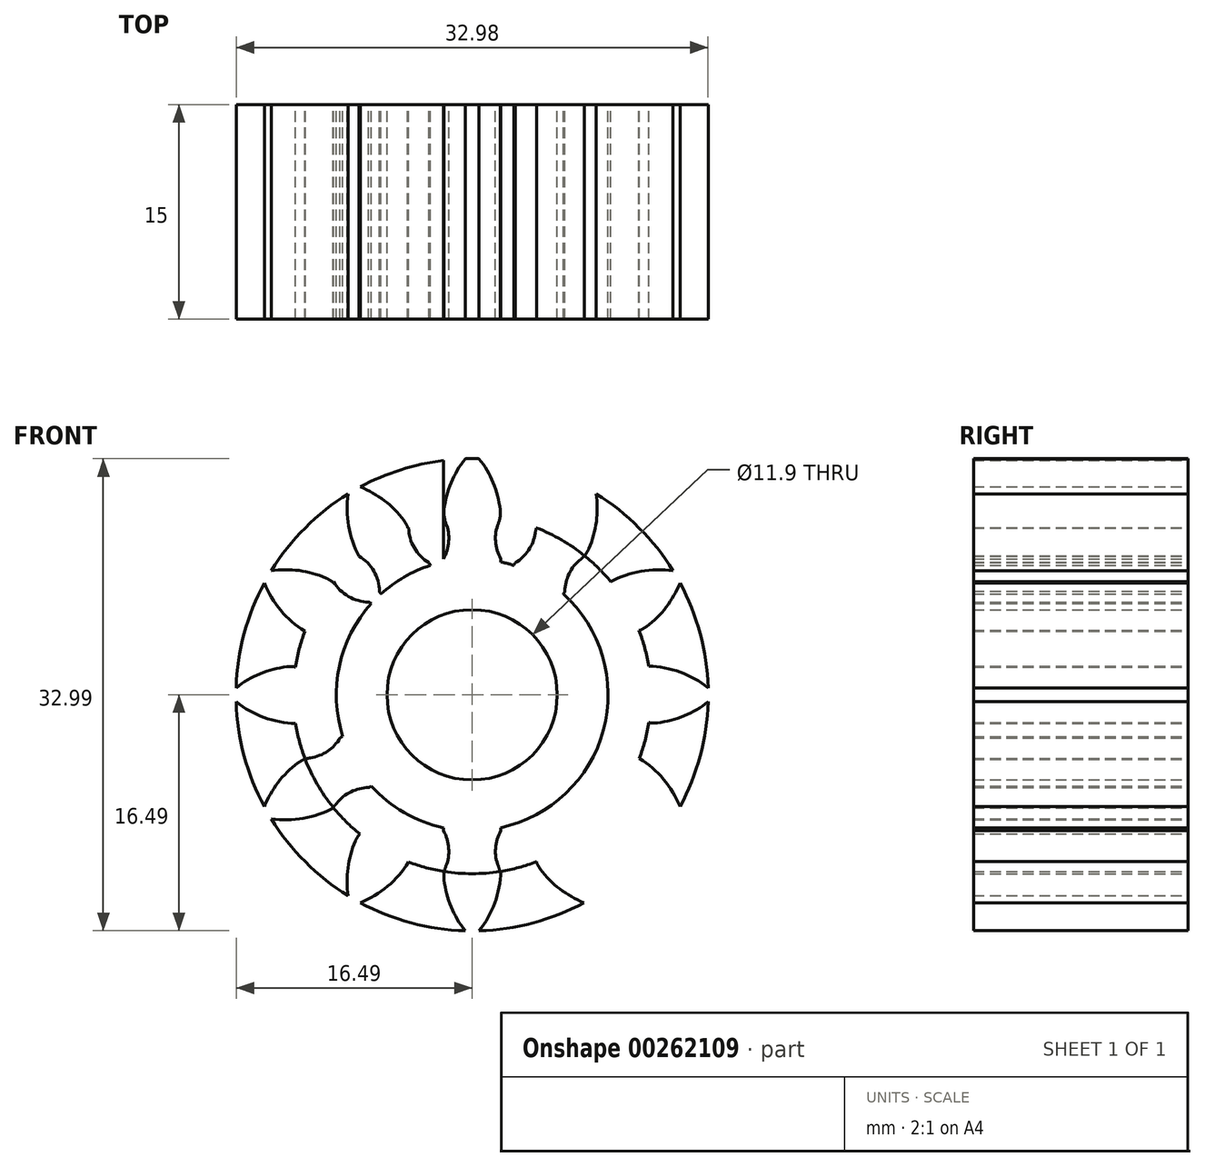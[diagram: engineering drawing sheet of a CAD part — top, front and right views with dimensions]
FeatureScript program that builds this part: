
annotation { "Feature Type Name" : "Feature", "Feature Type Description" : "" }
export const myFeature = defineFeature(function(context is Context, id is Id, definition is map)
    precondition{}
    {
        {
            var Q0;
            Q0=qCreatedBy(makeId("Front.planeOp"),FACE);
            var sketch = newSketch(context, id + "F0", { "sketchPlane" : qUnion([Q0])});
            skCircle(sketch, "E0", {"center": v(0, 0) * mm, "radius": 16.5 * mm});
            skCircle(sketch, "E1", {"center": v(0, 0) * mm, "radius": 9.5 * mm});
            skCircle(sketch, "E2", {"center": v(0, 0) * mm, "radius": 12.5 * mm});
            skLineSegment(sketch, "E3", {"start": v(0, 0) * mm, "end": v(0, 25.7) * mm, "construction": true});
            skLineSegment(sketch, "E4", {"start": v(0, 12.5) * mm, "end": v(10.82, 16.44) * mm});
            skLineSegment(sketch, "E5", {"start": v(0, 12.5) * mm, "end": v(18.32, 12.5) * mm, "construction": true});
            skLineSegment(sketch, "E6", {"start": v(0, 9.5) * mm, "end": v(-2, 9.5) * mm, "construction": true});
            skLineSegment(sketch, "E7", {"start": v(-2, 9.5) * mm, "end": v(-2, 16.38) * mm});
            skLineSegment(sketch, "E8.MirrorCS", {"start": v(2, 9.5) * mm, "end": v(2, 16.38) * mm});
            skLineSegment(sketch, "E9", {"start": v(-2, 12.34) * mm, "end": v(-5.78, 12.34) * mm, "construction": true});
            skArc(sketch, "E10.MirrorCS", {"start": v(0.49, 16.5) * mm, "mid": v(1.47, 14.82) * mm, "end": v(1.96, 12.94) * mm});
            skArc(sketch, "E11.MirrorCS", {"start": v(0.49, 16.5) * mm, "mid": v(1.42, 14.94) * mm, "end": v(1.92, 13.2) * mm});
            skArc(sketch, "E12", {"start": v(-2, 9.5) * mm, "mid": v(-1.64, 10.72) * mm, "end": v(-1.83, 11.98) * mm});
            skArc(sketch, "E13.MirrorCS", {"start": v(2, 9.5) * mm, "mid": v(1.64, 10.72) * mm, "end": v(1.83, 11.98) * mm});
            skArc(sketch, "E14.1.0", {"start": v(-6.48, 7.23) * mm, "mid": v(-6.87, 8.64) * mm, "end": v(-7.9, 9.69) * mm});
            skArc(sketch, "E14.1.1", {"start": v(-3.02, 9.23) * mm, "mid": v(-4.05, 10.27) * mm, "end": v(-4.44, 11.69) * mm});
            skArc(sketch, "E14.2.0", {"start": v(-9.23, 3.02) * mm, "mid": v(-10.27, 4.05) * mm, "end": v(-11.69, 4.44) * mm});
            skArc(sketch, "E14.2.1", {"start": v(-7.23, 6.48) * mm, "mid": v(-8.64, 6.87) * mm, "end": v(-9.69, 7.9) * mm});
            skArc(sketch, "E15.1.0", {"start": v(-6.48, -7.23) * mm, "mid": v(-6.87, -8.64) * mm, "end": v(-7.9, -9.69) * mm});
            skArc(sketch, "E15.1.2", {"start": v(-3.02, -9.23) * mm, "mid": v(-4.05, -10.27) * mm, "end": v(-4.44, -11.69) * mm});
            skArc(sketch, "E15.2.0", {"start": v(-2, -9.5) * mm, "mid": v(-1.63, -10.92) * mm, "end": v(-2, -12.34) * mm});
            skArc(sketch, "E16.8.3.0", {"start": v(6.48, -7.23) * mm, "mid": v(6.87, -8.64) * mm, "end": v(7.9, -9.69) * mm});
            skArc(sketch, "E16.14.3.0", {"start": v(3.02, -9.23) * mm, "mid": v(4.05, -10.27) * mm, "end": v(4.44, -11.69) * mm});
            skArc(sketch, "E16.4.4.0", {"start": v(14.04, -8.67) * mm, "mid": v(11.8, -8.64) * mm, "end": v(9.69, -7.9) * mm});
            skArc(sketch, "E16.8.4.0", {"start": v(9.23, -3.02) * mm, "mid": v(10.27, -4.05) * mm, "end": v(11.69, -4.44) * mm});
            skArc(sketch, "E16.14.4.0", {"start": v(7.23, -6.48) * mm, "mid": v(8.64, -6.87) * mm, "end": v(9.69, -7.9) * mm});
            skArc(sketch, "E16.8.5.0", {"start": v(9.5, 2) * mm, "mid": v(10.92, 1.63) * mm, "end": v(12.34, 2) * mm});
            skArc(sketch, "E16.14.5.0", {"start": v(9.5, -2) * mm, "mid": v(10.92, -1.63) * mm, "end": v(12.34, -2) * mm});
            skArc(sketch, "E16.8.6.0", {"start": v(7.23, 6.48) * mm, "mid": v(8.64, 6.87) * mm, "end": v(9.69, 7.9) * mm});
            skArc(sketch, "E16.14.6.0", {"start": v(9.23, 3.02) * mm, "mid": v(10.27, 4.05) * mm, "end": v(11.69, 4.44) * mm});
            skArc(sketch, "E16.14.7.0", {"start": v(6.48, 7.23) * mm, "mid": v(6.87, 8.64) * mm, "end": v(7.9, 9.69) * mm});
            skArc(sketch, "E16.8.11.0", {"start": v(-9.5, -2) * mm, "mid": v(-10.92, -1.63) * mm, "end": v(-12.34, -2) * mm});
            skArc(sketch, "E16.14.11.0", {"start": v(-9.5, 2) * mm, "mid": v(-10.92, 1.63) * mm, "end": v(-12.34, 2) * mm});
            skArc(sketch, "E17.1.2", {"start": v(-7.82, -14.53) * mm, "mid": v(-5.9, -13.38) * mm, "end": v(-4.44, -11.69) * mm});
            skArc(sketch, "E17.2.0", {"start": v(1.66, 14.47) * mm, "mid": v(2.03, 13.24) * mm, "end": v(1.83, 11.98) * mm});
            skPoint(sketch, "E18.visualSharp", {"position": v(-8.06, 20.68) * mm});
            skArc(sketch, "E18.filletArc", {"start": v(-1.96, 12.94) * mm, "mid": v(-1.95, 12.45) * mm, "end": v(-1.83, 11.98) * mm});
            skPoint(sketch, "E19.orphan", {"position": v(-2, 12.34) * mm});
            skPoint(sketch, "E20.visualSharp", {"position": v(2, 12.34) * mm});
            skArc(sketch, "E20.filletArc", {"start": v(1.83, 11.98) * mm, "mid": v(1.95, 12.45) * mm, "end": v(1.96, 12.94) * mm});
            skPoint(sketch, "E21.orphan", {"position": v(1.66, 11.63) * mm});
            skPoint(sketch, "E22.start.orphan", {"position": v(-0.49, 16.5) * mm});
            skArc(sketch, "E23.4.3.0", {"start": v(-16.5, 0.49) * mm, "mid": v(-14.94, 1.42) * mm, "end": v(-13.2, 1.92) * mm});
            skArc(sketch, "E23.8.3.0", {"start": v(-9.5, 2) * mm, "mid": v(-10.72, 1.64) * mm, "end": v(-11.98, 1.83) * mm});
            skPoint(sketch, "E23.11.3.0", {"position": v(-12.34, 2) * mm});
            skArc(sketch, "E23.12.3.0", {"start": v(-9.5, -2) * mm, "mid": v(-10.72, -1.64) * mm, "end": v(-11.98, -1.83) * mm});
            skArc(sketch, "E23.4.4.0", {"start": v(-14.53, -7.82) * mm, "mid": v(-13.65, -6.24) * mm, "end": v(-12.4, -4.93) * mm});
            skArc(sketch, "E23.8.4.0", {"start": v(-9.23, -3.02) * mm, "mid": v(-10.1, -3.94) * mm, "end": v(-11.3, -4.4) * mm});
            skPoint(sketch, "E23.11.4.0", {"position": v(-11.69, -4.44) * mm});
            skArc(sketch, "E23.12.4.0", {"start": v(-7.23, -6.48) * mm, "mid": v(-8.47, -6.78) * mm, "end": v(-9.46, -7.58) * mm});
            skArc(sketch, "E23.4.5.0", {"start": v(-8.67, -14.04) * mm, "mid": v(-8.7, -12.23) * mm, "end": v(-8.27, -10.47) * mm});
            skArc(sketch, "E23.8.5.0", {"start": v(-6.48, -7.23) * mm, "mid": v(-6.78, -8.47) * mm, "end": v(-7.58, -9.46) * mm});
            skPoint(sketch, "E23.11.5.0", {"position": v(-7.9, -9.69) * mm});
            skArc(sketch, "E23.12.5.0", {"start": v(-3.02, -9.23) * mm, "mid": v(-3.94, -10.1) * mm, "end": v(-4.4, -11.3) * mm});
            skArc(sketch, "E23.4.6.0", {"start": v(-0.49, -16.5) * mm, "mid": v(-1.42, -14.94) * mm, "end": v(-1.92, -13.2) * mm});
            skArc(sketch, "E23.8.6.0", {"start": v(-2, -9.5) * mm, "mid": v(-1.64, -10.72) * mm, "end": v(-1.83, -11.98) * mm});
            skPoint(sketch, "E23.11.6.0", {"position": v(-2, -12.34) * mm});
            skArc(sketch, "E23.12.6.0", {"start": v(2, -9.5) * mm, "mid": v(1.64, -10.72) * mm, "end": v(1.83, -11.98) * mm});
            skArc(sketch, "E23.4.7.0", {"start": v(7.82, -14.53) * mm, "mid": v(6.24, -13.65) * mm, "end": v(4.93, -12.4) * mm});
            skArc(sketch, "E23.8.7.0", {"start": v(3.02, -9.23) * mm, "mid": v(3.94, -10.1) * mm, "end": v(4.4, -11.3) * mm});
            skPoint(sketch, "E23.11.7.0", {"position": v(4.44, -11.69) * mm});
            skArc(sketch, "E23.12.7.0", {"start": v(6.48, -7.23) * mm, "mid": v(6.78, -8.47) * mm, "end": v(7.58, -9.46) * mm});
            skArc(sketch, "E23.4.8.0", {"start": v(14.04, -8.67) * mm, "mid": v(12.23, -8.7) * mm, "end": v(10.47, -8.27) * mm});
            skArc(sketch, "E23.8.8.0", {"start": v(7.23, -6.48) * mm, "mid": v(8.47, -6.78) * mm, "end": v(9.46, -7.58) * mm});
            skPoint(sketch, "E23.11.8.0", {"position": v(9.69, -7.9) * mm});
            skArc(sketch, "E23.12.8.0", {"start": v(9.23, -3.02) * mm, "mid": v(10.1, -3.94) * mm, "end": v(11.3, -4.4) * mm});
            skArc(sketch, "E23.4.9.0", {"start": v(16.5, -0.49) * mm, "mid": v(14.94, -1.42) * mm, "end": v(13.2, -1.92) * mm});
            skArc(sketch, "E23.8.9.0", {"start": v(9.5, -2) * mm, "mid": v(10.72, -1.64) * mm, "end": v(11.98, -1.83) * mm});
            skPoint(sketch, "E23.11.9.0", {"position": v(12.34, -2) * mm});
            skArc(sketch, "E23.12.9.0", {"start": v(9.5, 2) * mm, "mid": v(10.72, 1.64) * mm, "end": v(11.98, 1.83) * mm});
            skArc(sketch, "E23.4.10.0", {"start": v(14.53, 7.82) * mm, "mid": v(13.65, 6.24) * mm, "end": v(12.4, 4.93) * mm});
            skArc(sketch, "E23.8.10.0", {"start": v(9.23, 3.02) * mm, "mid": v(10.1, 3.94) * mm, "end": v(11.3, 4.4) * mm});
            skPoint(sketch, "E23.11.10.0", {"position": v(11.69, 4.44) * mm});
            skArc(sketch, "E23.12.10.0", {"start": v(7.23, 6.48) * mm, "mid": v(8.47, 6.78) * mm, "end": v(9.46, 7.58) * mm});
            skArc(sketch, "E23.4.11.0", {"start": v(8.67, 14.04) * mm, "mid": v(8.7, 12.23) * mm, "end": v(8.27, 10.47) * mm});
            skArc(sketch, "E23.8.11.0", {"start": v(6.48, 7.23) * mm, "mid": v(6.78, 8.47) * mm, "end": v(7.58, 9.46) * mm});
            skPoint(sketch, "E23.11.11.0", {"position": v(7.9, 9.69) * mm});
            skArc(sketch, "E23.12.11.0", {"start": v(3.02, 9.23) * mm, "mid": v(3.94, 10.1) * mm, "end": v(4.4, 11.3) * mm});
            skArc(sketch, "E24.4.3.0", {"start": v(-7.82, 14.53) * mm, "mid": v(-6.24, 13.65) * mm, "end": v(-4.93, 12.4) * mm});
            skArc(sketch, "E24.8.3.0", {"start": v(-14.04, -8.67) * mm, "mid": v(-11.8, -8.64) * mm, "end": v(-9.69, -7.9) * mm});
            skArc(sketch, "E24.4.4.0", {"start": v(-14.04, 8.67) * mm, "mid": v(-12.23, 8.7) * mm, "end": v(-10.47, 8.27) * mm});
            skArc(sketch, "E24.8.5.0", {"start": v(0.49, -16.5) * mm, "mid": v(1.58, -14.54) * mm, "end": v(2, -12.34) * mm});
            skArc(sketch, "E24.8.6.0", {"start": v(8.67, -14.04) * mm, "mid": v(8.64, -11.8) * mm, "end": v(7.9, -9.69) * mm});
            skArc(sketch, "E24.8.7.0", {"start": v(14.53, -7.82) * mm, "mid": v(13.38, -5.9) * mm, "end": v(11.69, -4.44) * mm});
            skArc(sketch, "E24.12.7.0", {"start": v(3.02, 9.23) * mm, "mid": v(4.05, 10.27) * mm, "end": v(4.44, 11.69) * mm});
            skArc(sketch, "E24.8.8.0", {"start": v(16.5, 0.49) * mm, "mid": v(14.54, 1.58) * mm, "end": v(12.34, 2) * mm});
            skArc(sketch, "E24.10.8.0", {"start": v(2, 9.5) * mm, "mid": v(1.63, 10.92) * mm, "end": v(2, 12.34) * mm});
            skArc(sketch, "E24.12.8.0", {"start": v(-2, 9.5) * mm, "mid": v(-1.63, 10.92) * mm, "end": v(-2, 12.34) * mm});
            skArc(sketch, "E24.8.9.0", {"start": v(14.04, 8.67) * mm, "mid": v(11.8, 8.64) * mm, "end": v(9.69, 7.9) * mm});
            skArc(sketch, "E24.8.10.0", {"start": v(7.82, 14.53) * mm, "mid": v(5.9, 13.38) * mm, "end": v(4.44, 11.69) * mm});
            skArc(sketch, "E24.8.11.0", {"start": v(-0.49, 16.5) * mm, "mid": v(-1.58, 14.54) * mm, "end": v(-2, 12.34) * mm});
            skArc(sketch, "E25.1.2", {"start": v(-8.17, 10.23) * mm, "mid": v(-7.92, 9.8) * mm, "end": v(-7.58, 9.46) * mm});
            skArc(sketch, "E25.1.3", {"start": v(-4.4, 11.3) * mm, "mid": v(-4.54, 11.76) * mm, "end": v(-4.78, 12.19) * mm});
            skArc(sketch, "E25.1.4", {"start": v(-7.82, 14.53) * mm, "mid": v(-6.14, 13.57) * mm, "end": v(-4.78, 12.19) * mm});
            skArc(sketch, "E25.1.5", {"start": v(-8.67, 14.04) * mm, "mid": v(-8.64, 11.8) * mm, "end": v(-7.9, 9.69) * mm});
            skArc(sketch, "E25.2.2", {"start": v(-12.19, 4.78) * mm, "mid": v(-11.76, 4.54) * mm, "end": v(-11.3, 4.4) * mm});
            skArc(sketch, "E25.2.3", {"start": v(-9.46, 7.58) * mm, "mid": v(-9.8, 7.92) * mm, "end": v(-10.23, 8.17) * mm});
            skArc(sketch, "E25.2.4", {"start": v(-14.04, 8.67) * mm, "mid": v(-12.1, 8.68) * mm, "end": v(-10.23, 8.17) * mm});
            skArc(sketch, "E25.2.5", {"start": v(-14.53, 7.82) * mm, "mid": v(-13.38, 5.9) * mm, "end": v(-11.69, 4.44) * mm});
            skArc(sketch, "E25.3.2", {"start": v(-12.94, -1.96) * mm, "mid": v(-12.45, -1.95) * mm, "end": v(-11.98, -1.83) * mm});
            skArc(sketch, "E25.3.3", {"start": v(-11.98, 1.83) * mm, "mid": v(-12.45, 1.95) * mm, "end": v(-12.94, 1.96) * mm});
            skArc(sketch, "E25.3.4", {"start": v(-16.5, 0.49) * mm, "mid": v(-14.82, 1.47) * mm, "end": v(-12.94, 1.96) * mm});
            skArc(sketch, "E25.3.5", {"start": v(-16.5, -0.49) * mm, "mid": v(-14.54, -1.58) * mm, "end": v(-12.34, -2) * mm});
            skArc(sketch, "E25.4.2", {"start": v(-10.23, -8.17) * mm, "mid": v(-9.8, -7.92) * mm, "end": v(-9.46, -7.58) * mm});
            skArc(sketch, "E25.4.3", {"start": v(-11.3, -4.4) * mm, "mid": v(-11.76, -4.54) * mm, "end": v(-12.19, -4.78) * mm});
            skArc(sketch, "E25.4.4", {"start": v(-14.53, -7.82) * mm, "mid": v(-13.57, -6.14) * mm, "end": v(-12.19, -4.78) * mm});
            skArc(sketch, "E25.5.2", {"start": v(-4.78, -12.19) * mm, "mid": v(-4.54, -11.76) * mm, "end": v(-4.4, -11.3) * mm});
            skArc(sketch, "E25.5.3", {"start": v(-7.58, -9.46) * mm, "mid": v(-7.92, -9.8) * mm, "end": v(-8.17, -10.23) * mm});
            skArc(sketch, "E25.5.4", {"start": v(-8.67, -14.04) * mm, "mid": v(-8.68, -12.1) * mm, "end": v(-8.17, -10.23) * mm});
            skArc(sketch, "E25.6.2", {"start": v(1.96, -12.94) * mm, "mid": v(1.95, -12.45) * mm, "end": v(1.83, -11.98) * mm});
            skArc(sketch, "E25.6.3", {"start": v(-1.83, -11.98) * mm, "mid": v(-1.95, -12.45) * mm, "end": v(-1.96, -12.94) * mm});
            skArc(sketch, "E25.6.4", {"start": v(-0.49, -16.5) * mm, "mid": v(-1.47, -14.82) * mm, "end": v(-1.96, -12.94) * mm});
            skArc(sketch, "E25.7.2", {"start": v(8.17, -10.23) * mm, "mid": v(7.92, -9.8) * mm, "end": v(7.58, -9.46) * mm});
            skArc(sketch, "E25.7.3", {"start": v(4.4, -11.3) * mm, "mid": v(4.54, -11.76) * mm, "end": v(4.78, -12.19) * mm});
            skArc(sketch, "E25.7.4", {"start": v(7.82, -14.53) * mm, "mid": v(6.14, -13.57) * mm, "end": v(4.78, -12.19) * mm});
            skArc(sketch, "E25.8.2", {"start": v(12.19, -4.78) * mm, "mid": v(11.76, -4.54) * mm, "end": v(11.3, -4.4) * mm});
            skArc(sketch, "E25.8.3", {"start": v(9.46, -7.58) * mm, "mid": v(9.8, -7.92) * mm, "end": v(10.23, -8.17) * mm});
            skArc(sketch, "E25.8.4", {"start": v(14.04, -8.67) * mm, "mid": v(12.1, -8.68) * mm, "end": v(10.23, -8.17) * mm});
            skArc(sketch, "E25.9.2", {"start": v(12.94, 1.96) * mm, "mid": v(12.45, 1.95) * mm, "end": v(11.98, 1.83) * mm});
            skArc(sketch, "E25.9.3", {"start": v(11.98, -1.83) * mm, "mid": v(12.45, -1.95) * mm, "end": v(12.94, -1.96) * mm});
            skArc(sketch, "E25.9.4", {"start": v(16.5, -0.49) * mm, "mid": v(14.82, -1.47) * mm, "end": v(12.94, -1.96) * mm});
            skArc(sketch, "E25.10.2", {"start": v(10.23, 8.17) * mm, "mid": v(9.8, 7.92) * mm, "end": v(9.46, 7.58) * mm});
            skArc(sketch, "E25.10.3", {"start": v(11.3, 4.4) * mm, "mid": v(11.76, 4.54) * mm, "end": v(12.19, 4.78) * mm});
            skArc(sketch, "E25.10.4", {"start": v(14.53, 7.82) * mm, "mid": v(13.57, 6.14) * mm, "end": v(12.19, 4.78) * mm});
            skArc(sketch, "E25.11.2", {"start": v(4.78, 12.19) * mm, "mid": v(4.54, 11.76) * mm, "end": v(4.4, 11.3) * mm});
            skArc(sketch, "E25.11.3", {"start": v(7.58, 9.46) * mm, "mid": v(7.92, 9.8) * mm, "end": v(8.17, 10.23) * mm});
            skArc(sketch, "E25.11.4", {"start": v(8.67, 14.04) * mm, "mid": v(8.68, 12.1) * mm, "end": v(8.17, 10.23) * mm});
            skArc(sketch, "E26", {"start": v(-2, 9.5) * mm, "mid": v(-2, 9.4) * mm, "end": v(-2, 9.29) * mm});
            skArc(sketch, "E27.MirrorCS", {"start": v(2, 9.5) * mm, "mid": v(2, 9.4) * mm, "end": v(2, 9.29) * mm});
            skArc(sketch, "E28.1.0", {"start": v(-3.02, 9.23) * mm, "mid": v(-2.96, 9.14) * mm, "end": v(-2.91, 9.04) * mm});
            skArc(sketch, "E28.1.1", {"start": v(-6.48, 7.23) * mm, "mid": v(-6.44, 7.13) * mm, "end": v(-6.38, 7.04) * mm});
            skArc(sketch, "E28.2.0", {"start": v(-7.23, 6.48) * mm, "mid": v(-7.13, 6.44) * mm, "end": v(-7.04, 6.38) * mm});
            skArc(sketch, "E28.2.1", {"start": v(-9.23, 3.02) * mm, "mid": v(-9.14, 2.96) * mm, "end": v(-9.04, 2.91) * mm});
            skArc(sketch, "E28.3.0", {"start": v(-9.5, 2) * mm, "mid": v(-9.4, 2) * mm, "end": v(-9.29, 2) * mm});
            skArc(sketch, "E28.3.1", {"start": v(-9.5, -2) * mm, "mid": v(-9.4, -2) * mm, "end": v(-9.29, -2) * mm});
            skArc(sketch, "E28.4.0", {"start": v(-9.23, -3.02) * mm, "mid": v(-9.14, -2.96) * mm, "end": v(-9.04, -2.91) * mm});
            skArc(sketch, "E28.4.1", {"start": v(-7.23, -6.48) * mm, "mid": v(-7.13, -6.44) * mm, "end": v(-7.04, -6.38) * mm});
            skArc(sketch, "E28.5.0", {"start": v(-6.48, -7.23) * mm, "mid": v(-6.44, -7.13) * mm, "end": v(-6.38, -7.04) * mm});
            skArc(sketch, "E28.5.1", {"start": v(-3.02, -9.23) * mm, "mid": v(-2.96, -9.14) * mm, "end": v(-2.91, -9.04) * mm});
            skArc(sketch, "E28.6.0", {"start": v(-2, -9.5) * mm, "mid": v(-2, -9.4) * mm, "end": v(-2, -9.29) * mm});
            skArc(sketch, "E28.6.1", {"start": v(2, -9.5) * mm, "mid": v(2, -9.4) * mm, "end": v(2, -9.29) * mm});
            skArc(sketch, "E28.7.0", {"start": v(3.02, -9.23) * mm, "mid": v(2.96, -9.14) * mm, "end": v(2.91, -9.04) * mm});
            skArc(sketch, "E28.7.1", {"start": v(6.48, -7.23) * mm, "mid": v(6.44, -7.13) * mm, "end": v(6.38, -7.04) * mm});
            skArc(sketch, "E28.8.0", {"start": v(7.23, -6.48) * mm, "mid": v(7.13, -6.44) * mm, "end": v(7.04, -6.38) * mm});
            skArc(sketch, "E28.8.1", {"start": v(9.23, -3.02) * mm, "mid": v(9.14, -2.96) * mm, "end": v(9.04, -2.91) * mm});
            skArc(sketch, "E28.9.0", {"start": v(9.5, -2) * mm, "mid": v(9.4, -2) * mm, "end": v(9.29, -2) * mm});
            skArc(sketch, "E28.9.1", {"start": v(9.5, 2) * mm, "mid": v(9.4, 2) * mm, "end": v(9.29, 2) * mm});
            skArc(sketch, "E28.10.0", {"start": v(9.23, 3.02) * mm, "mid": v(9.14, 2.96) * mm, "end": v(9.04, 2.91) * mm});
            skArc(sketch, "E28.10.1", {"start": v(7.23, 6.48) * mm, "mid": v(7.13, 6.44) * mm, "end": v(7.04, 6.38) * mm});
            skArc(sketch, "E28.11.0", {"start": v(6.48, 7.23) * mm, "mid": v(6.44, 7.13) * mm, "end": v(6.38, 7.04) * mm});
            skArc(sketch, "E28.11.1", {"start": v(3.02, 9.23) * mm, "mid": v(2.96, 9.14) * mm, "end": v(2.91, 9.04) * mm});
            skCircle(sketch, "E29", {"center": v(0, 0) * mm, "radius": 5.95 * mm});
            skSolve(sketch);
        }
        {
            var Q0;
            Q0=makeQuery(id+"F0.imprint","IMPRINT",FACE,{"disambiguationData":[TD([[makeQuery(id+"F0.imprint","IMPRINT",EDGE,{"derivedFrom":sQuery(id+"F0.wireOp",EDGE,"E29")}),-1.0]])]});
            var Q1;
            {var subQ5=sQuery(id+"F0.wireOp",EDGE,"E28.2.0");Q1=makeQuery(id+"F0.imprint","IMPRINT",FACE,{"disambiguationData":[TD([[makeQuery(id+"F0.imprint","IMPRINT",EDGE,{"derivedFrom":subQ5}),-1.0]])]});}
            var Q2;
            {var subQ6=sQuery(id+"F0.wireOp",EDGE,"E28.1.0");Q2=makeQuery(id+"F0.imprint","IMPRINT",FACE,{"disambiguationData":[TD([[makeQuery(id+"F0.imprint","IMPRINT",EDGE,{"derivedFrom":subQ6}),-1.0]])]});}
            var Q3;
            {var subQ11=sQuery(id+"F0.wireOp",EDGE,"E26");Q3=makeQuery(id+"F0.imprint","IMPRINT",FACE,{"disambiguationData":[TD([[makeQuery(id+"F0.imprint","IMPRINT",EDGE,{"derivedFrom":subQ11}),1.0]])]});}
            var Q4;
            {var subQ1=sQuery(id+"F0.wireOp",EDGE,"E23.12.11.0");Q4=makeQuery(id+"F0.imprint","IMPRINT",FACE,{"disambiguationData":[TD([[makeQuery(id+"F0.imprint","IMPRINT",EDGE,{"derivedFrom":subQ1}),-1.0]])]});}
            var Q5;
            {var subQ1=sQuery(id+"F0.wireOp",EDGE,"E23.12.10.0");Q5=makeQuery(id+"F0.imprint","IMPRINT",FACE,{"disambiguationData":[TD([[makeQuery(id+"F0.imprint","IMPRINT",EDGE,{"derivedFrom":subQ1}),-1.0]])]});}
            var Q6;
            {var subQ1=sQuery(id+"F0.wireOp",EDGE,"E23.12.9.0");Q6=makeQuery(id+"F0.imprint","IMPRINT",FACE,{"disambiguationData":[TD([[makeQuery(id+"F0.imprint","IMPRINT",EDGE,{"derivedFrom":subQ1}),-1.0]])]});}
            var Q7;
            {var subQ1=sQuery(id+"F0.wireOp",EDGE,"E23.12.8.0");Q7=makeQuery(id+"F0.imprint","IMPRINT",FACE,{"disambiguationData":[TD([[makeQuery(id+"F0.imprint","IMPRINT",EDGE,{"derivedFrom":subQ1}),-1.0]])]});}
            var Q8;
            {var subQ2=sQuery(id+"F0.wireOp",EDGE,"E23.12.7.0");Q8=makeQuery(id+"F0.imprint","IMPRINT",FACE,{"disambiguationData":[TD([[makeQuery(id+"F0.imprint","IMPRINT",EDGE,{"derivedFrom":subQ2}),-1.0]])]});}
            var Q9;
            {var subQ1=sQuery(id+"F0.wireOp",EDGE,"E23.12.6.0");Q9=makeQuery(id+"F0.imprint","IMPRINT",FACE,{"disambiguationData":[TD([[makeQuery(id+"F0.imprint","IMPRINT",EDGE,{"derivedFrom":subQ1}),-1.0]])]});}
            var Q10;
            {var subQ1=sQuery(id+"F0.wireOp",EDGE,"E23.12.5.0");Q10=makeQuery(id+"F0.imprint","IMPRINT",FACE,{"disambiguationData":[TD([[makeQuery(id+"F0.imprint","IMPRINT",EDGE,{"derivedFrom":subQ1}),-1.0]])]});}
            var Q11;
            {var subQ1=sQuery(id+"F0.wireOp",EDGE,"E23.12.4.0");Q11=makeQuery(id+"F0.imprint","IMPRINT",FACE,{"disambiguationData":[TD([[makeQuery(id+"F0.imprint","IMPRINT",EDGE,{"derivedFrom":subQ1}),-1.0]])]});}
            var Q12;
            {var subQ1=sQuery(id+"F0.wireOp",EDGE,"E23.12.3.0");Q12=makeQuery(id+"F0.imprint","IMPRINT",FACE,{"disambiguationData":[TD([[makeQuery(id+"F0.imprint","IMPRINT",EDGE,{"derivedFrom":subQ1}),-1.0]])]});}
            var Q13;
            {var subQ0=sQuery(id+"F0.wireOp",EDGE,"E25.3.4");var subQ12=makeQuery(id+"F0.imprint","IMPRINT",VERTEX,{"derivedFrom":subQ0});Q13=makeQuery(id+"F0.imprint","IMPRINT",FACE,{"disambiguationData":[TD([[makeQuery(id+"F0.imprint","IMPRINT",EDGE,{"disambiguationData":[TD([[subQ12,1.0]])],"derivedFrom":subQ0}),-1.0]])]});}
            var Q14;
            {var subQ0=sQuery(id+"F0.wireOp",EDGE,"E25.2.4");var subQ12=makeQuery(id+"F0.imprint","IMPRINT",VERTEX,{"derivedFrom":subQ0});Q14=makeQuery(id+"F0.imprint","IMPRINT",FACE,{"disambiguationData":[TD([[makeQuery(id+"F0.imprint","IMPRINT",EDGE,{"disambiguationData":[TD([[subQ12,1.0]])],"derivedFrom":subQ0}),-1.0]])]});}
            var Q15;
            {var subQ0=sQuery(id+"F0.wireOp",EDGE,"E25.1.4");var subQ12=makeQuery(id+"F0.imprint","IMPRINT",VERTEX,{"derivedFrom":subQ0});Q15=makeQuery(id+"F0.imprint","IMPRINT",FACE,{"disambiguationData":[TD([[makeQuery(id+"F0.imprint","IMPRINT",EDGE,{"disambiguationData":[TD([[subQ12,1.0]])],"derivedFrom":subQ0}),-1.0]])]});}
            var Q16;
            {var subQ3=sQuery(id+"F0.wireOp",EDGE,"E2");var subQ5=sQuery(id+"F0.wireOp",EDGE,"E4");var subQ6=makeQuery(id+"F0.imprint","INTERSECT",VERTEX,{"derivedFrom":[subQ3,subQ5]});Q16=makeQuery(id+"F0.imprint","IMPRINT",FACE,{"disambiguationData":[TD([[makeQuery(id+"F0.imprint","IMPRINT",EDGE,{"disambiguationData":[TD([[subQ6,-1.0]])],"derivedFrom":subQ3}),-1.0]])]});}
            var Q17;
            {var subQ0=sQuery(id+"F0.wireOp",EDGE,"E25.11.4");var subQ12=makeQuery(id+"F0.imprint","IMPRINT",VERTEX,{"derivedFrom":subQ0});Q17=makeQuery(id+"F0.imprint","IMPRINT",FACE,{"disambiguationData":[TD([[makeQuery(id+"F0.imprint","IMPRINT",EDGE,{"disambiguationData":[TD([[subQ12,1.0]])],"derivedFrom":subQ0}),-1.0]])]});}
            var Q18;
            {var subQ5=sQuery(id+"F0.wireOp",EDGE,"E25.10.4");var subQ12=makeQuery(id+"F0.imprint","IMPRINT",VERTEX,{"derivedFrom":subQ5});Q18=makeQuery(id+"F0.imprint","IMPRINT",FACE,{"disambiguationData":[TD([[makeQuery(id+"F0.imprint","IMPRINT",EDGE,{"disambiguationData":[TD([[subQ12,1.0]])],"derivedFrom":subQ5}),-1.0]])]});}
            var Q19;
            {var subQ0=sQuery(id+"F0.wireOp",EDGE,"E25.9.4");var subQ12=makeQuery(id+"F0.imprint","IMPRINT",VERTEX,{"derivedFrom":subQ0});Q19=makeQuery(id+"F0.imprint","IMPRINT",FACE,{"disambiguationData":[TD([[makeQuery(id+"F0.imprint","IMPRINT",EDGE,{"disambiguationData":[TD([[subQ12,1.0]])],"derivedFrom":subQ0}),-1.0]])]});}
            var Q20;
            {var subQ0=sQuery(id+"F0.wireOp",EDGE,"E25.8.4");var subQ12=makeQuery(id+"F0.imprint","IMPRINT",VERTEX,{"derivedFrom":subQ0});Q20=makeQuery(id+"F0.imprint","IMPRINT",FACE,{"disambiguationData":[TD([[makeQuery(id+"F0.imprint","IMPRINT",EDGE,{"disambiguationData":[TD([[subQ12,1.0]])],"derivedFrom":subQ0}),-1.0]])]});}
            var Q21;
            {var subQ0=sQuery(id+"F0.wireOp",EDGE,"E25.7.4");var subQ12=makeQuery(id+"F0.imprint","IMPRINT",VERTEX,{"derivedFrom":subQ0});Q21=makeQuery(id+"F0.imprint","IMPRINT",FACE,{"disambiguationData":[TD([[makeQuery(id+"F0.imprint","IMPRINT",EDGE,{"disambiguationData":[TD([[subQ12,1.0]])],"derivedFrom":subQ0}),-1.0]])]});}
            var Q22;
            {var subQ0=sQuery(id+"F0.wireOp",EDGE,"E25.6.4");var subQ9=makeQuery(id+"F0.imprint","IMPRINT",VERTEX,{"derivedFrom":subQ0});Q22=makeQuery(id+"F0.imprint","IMPRINT",FACE,{"disambiguationData":[TD([[makeQuery(id+"F0.imprint","IMPRINT",EDGE,{"disambiguationData":[TD([[subQ9,1.0]])],"derivedFrom":subQ0}),-1.0]])]});}
            var Q23;
            {var subQ0=sQuery(id+"F0.wireOp",EDGE,"E25.5.4");var subQ12=makeQuery(id+"F0.imprint","IMPRINT",VERTEX,{"derivedFrom":subQ0});Q23=makeQuery(id+"F0.imprint","IMPRINT",FACE,{"disambiguationData":[TD([[makeQuery(id+"F0.imprint","IMPRINT",EDGE,{"disambiguationData":[TD([[subQ12,1.0]])],"derivedFrom":subQ0}),-1.0]])]});}
            var Q24;
            {var subQ0=sQuery(id+"F0.wireOp",EDGE,"E25.4.4");var subQ12=makeQuery(id+"F0.imprint","IMPRINT",VERTEX,{"derivedFrom":subQ0});Q24=makeQuery(id+"F0.imprint","IMPRINT",FACE,{"disambiguationData":[TD([[makeQuery(id+"F0.imprint","IMPRINT",EDGE,{"disambiguationData":[TD([[subQ12,1.0]])],"derivedFrom":subQ0}),-1.0]])]});}
            var Q25;
            {var subQ0=sQuery(id+"F0.wireOp",EDGE,"E4");var subQ1=sQuery(id+"F0.wireOp",EDGE,"E2");var subQ2=makeQuery(id+"F0.imprint","INTERSECT",VERTEX,{"derivedFrom":[subQ1,subQ0]});Q25=makeQuery(id+"F0.imprint","IMPRINT",FACE,{"disambiguationData":[TD([[makeQuery(id+"F0.imprint","IMPRINT",EDGE,{"disambiguationData":[TD([[subQ2,1.0]])],"derivedFrom":subQ1}),-1.0]])]});}
            extrude(context, id + "F1", {"entities" : qUnion([Q0, Q1, Q2, Q3, Q4, Q5, Q6, Q7, Q8, Q9, Q10, Q11, Q12, Q13, Q14, Q15, Q16, Q17, Q18, Q19, Q20, Q21, Q22, Q23, Q24, Q25]), "depth" : 15 * mm});
        }
    });
